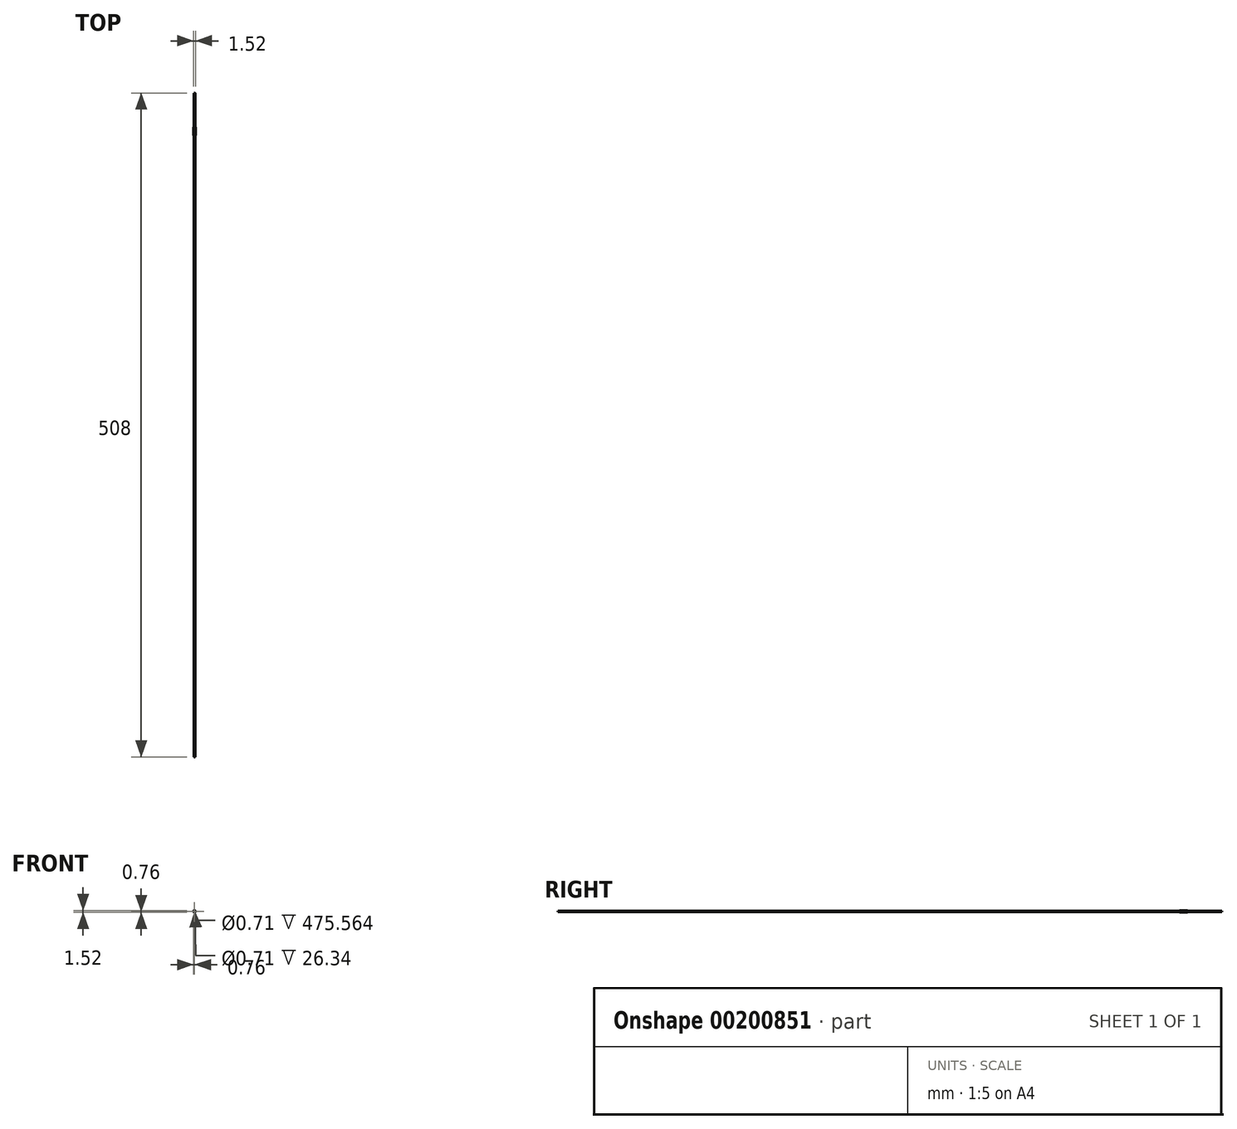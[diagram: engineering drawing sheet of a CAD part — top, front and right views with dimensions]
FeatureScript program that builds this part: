
annotation { "Feature Type Name" : "Feature", "Feature Type Description" : "" }
export const myFeature = defineFeature(function(context is Context, id is Id, definition is map)
    precondition{}
    {
        {
            var Q0;
            Q0=qCreatedBy(makeId("Front.planeOp"),FACE);
            var sketch = newSketch(context, id + "F0", { "sketchPlane" : qUnion([Q0])});
            skCircle(sketch, "E0", {"center": v(0, 0) * mm, "radius": 0.36 * mm});
            skCircle(sketch, "E1", {"center": v(0, 0) * mm, "radius": 0.43 * mm});
            skSolve(sketch);
        }
        {
            var Q0;
            Q0 = qSketchRegion(id + "F0", true);
            extrude(context, id + "F1", {"entities" : qUnion([Q0]), "depth" : 508 * mm});
        }
        {
            var Q0;
            Q0=qCreatedBy(makeId("Front.planeOp"),FACE);
            cPlane(context, id + "F2", {"entities" : qUnion([Q0]), "cplaneType" : CPlaneType.OFFSET, "offset" : 26.34 * mm, "width" : 152.4 * mm, "height" : 152.4 * mm});
        }
        {
            var Q0;
            Q0=qCreatedBy(id+"F2.planeOp",FACE);
            var sketch = newSketch(context, id + "F3", { "sketchPlane" : qUnion([Q0])});
            skCircle(sketch, "E2", {"center": v(0, 0) * mm, "radius": 0.76 * mm});
            skSolve(sketch);
        }
        {
            var Q0;
            Q0 = qSketchRegion(id + "F3", true);
            extrude(context, id + "F4", {"entities" : qUnion([Q0]), "operationType" : NewBodyOperationType.ADD, "depth" : 6.1 * mm});
        }
    });
